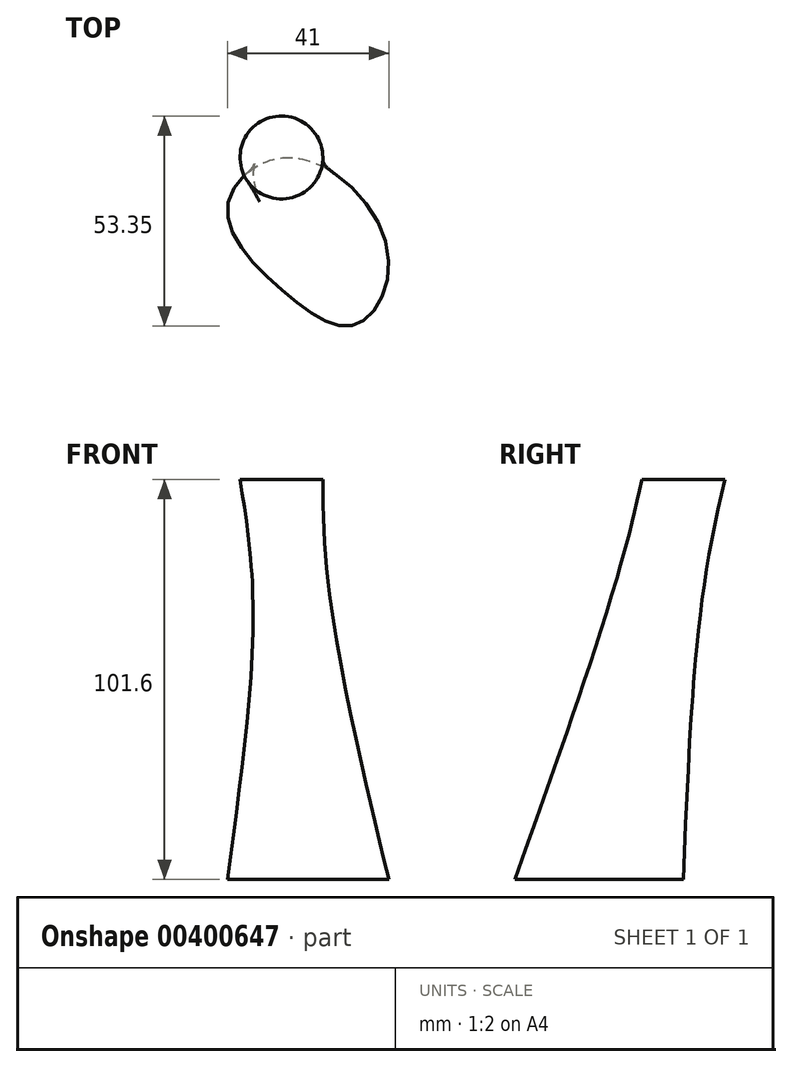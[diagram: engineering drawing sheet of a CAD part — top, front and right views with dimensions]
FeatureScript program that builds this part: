
annotation { "Feature Type Name" : "Feature", "Feature Type Description" : "" }
export const myFeature = defineFeature(function(context is Context, id is Id, definition is map)
    precondition{}
    {
        {
            var Q0;
            Q0=qCreatedBy(makeId("Top.planeOp"),FACE);
            cPlane(context, id + "F0", {"entities" : qUnion([Q0]), "cplaneType" : CPlaneType.OFFSET, "offset" : 101.6 * mm, "width" : 152.4 * mm, "height" : 152.4 * mm});
        }
        {
            var Q0;
            Q0=qCreatedBy(id+"F0.planeOp",FACE);
            var sketch = newSketch(context, id + "F1", { "sketchPlane" : qUnion([Q0])});
            skCircle(sketch, "E0", {"center": v(-61.88, 0) * mm, "radius": 10.52 * mm});
            skSolve(sketch);
        }
        {
            var Q0;
            Q0=qCreatedBy(makeId("Top.planeOp"),FACE);
            var sketch = newSketch(context, id + "F2", { "sketchPlane" : qUnion([Q0])});
            skFitSpline(sketch, "E1", {"points": [v(-60.85, -34.42) * mm, v(-75.56, -12.6) * mm, v(-59.43, 0) * mm, v(-35, -23.03) * mm, v(-42.86, -42.37) * mm, v(-60.85, -34.42) * mm]});
            skSolve(sketch);
        }
        {
            var Q0;
            Q0 = qSketchRegion(id + "F1", true);
            var Q1;
            Q1 = qSketchRegion(id + "F2", true);
            loft(context, id + "F3", {"sheetProfilesArray" : [{ "sheetProfileEntities" : qUnion([Q0]) }, { "sheetProfileEntities" : qUnion([Q1]) }]});
        }
    });
